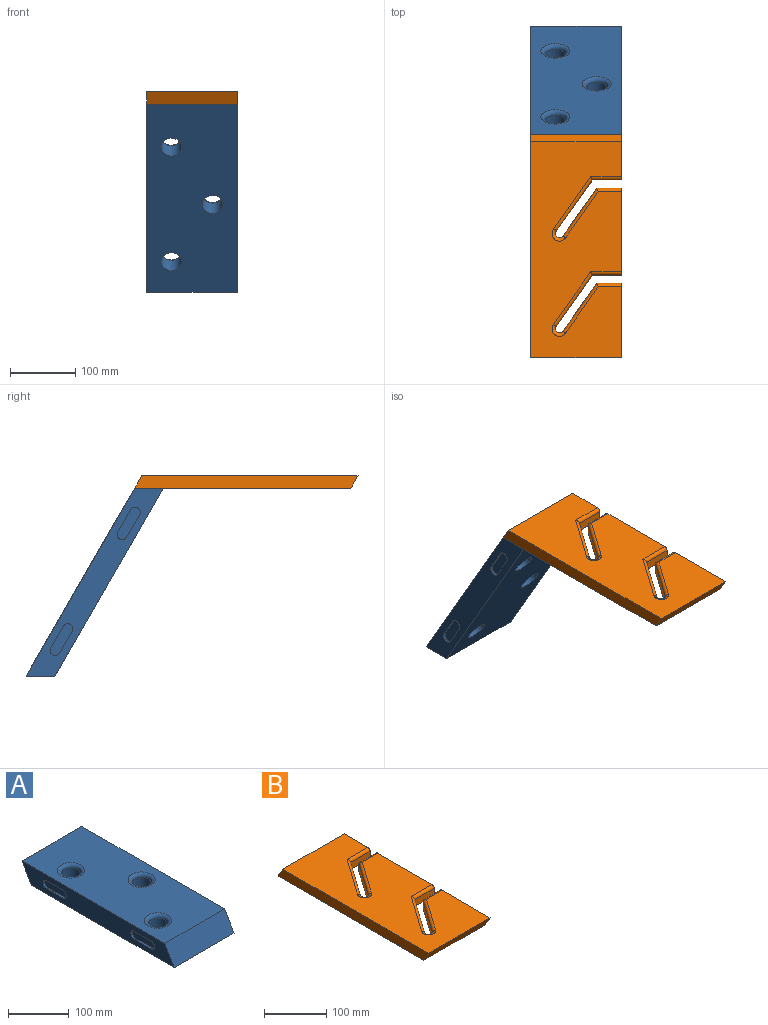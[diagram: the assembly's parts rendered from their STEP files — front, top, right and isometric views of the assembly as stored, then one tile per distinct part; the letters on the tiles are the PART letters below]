
ASSEMBLY  parts=2 mates=1
PART A: 22 faces, bbox 139.7x355.6x38.1 mm
  f0: plane 355.6x38.1mm, normal (-1,0,0), area 11085.4mm2, adj f1,f3,f4,f5,f6,f7,f8,f9
  f1: plane 333.6x139.7mm, normal (0,0,-1), area 44229.1mm2, adj f0,f2,f4,f5,f16,f17,f18
  f2: plane 355.6x38.1mm, normal (1,0,0), area 12710.3mm2, adj f1,f3,f4,f5
  f3: plane 333.6x139.7mm, normal (0,0,1), area 41949mm2, adj f0,f2,f4,f5,f19,f20,f21
  f4: plane 139.7x38.1mm, normal (0,-0.87,0.5), area 6146mm2, adj f0,f1,f2,f3
  f5: plane 139.7x38.1mm, normal (0,0.87,-0.5), area 6146mm2, adj f0,f1,f2,f3
  f6: cylinder r=7.95mm len=15.9mm, axis (-1,0,0), area 83mm2, adj f0,f7,f9,f10
  f7: plane 38.1x3.18mm, normal (0,0,1), area 121mm2, adj f0,f6,f8,f10
  f8: cylinder r=7.95mm len=15.9mm, axis (-1,0,0), area 83mm2, adj f0,f7,f9,f10
  f9: plane 38.1x3.18mm, normal (0,0,-1), area 121mm2, adj f0,f6,f8,f10
  f10: plane 55.17x15.91mm, normal (-1,0,0), area 821.4mm2, adj f6,f7,f8,f9
  f11: cylinder r=7.94mm len=15.88mm, axis (-1,0,0), area 79.1mm2, adj f0,f12,f14,f15
  f12: plane 38.1x3.18mm, normal (0,0,1), area 121mm2, adj f0,f11,f13,f15
  f13: cylinder r=7.95mm len=15.9mm, axis (-1,0,0), area 79.3mm2, adj f0,f12,f14,f15
  f14: plane 38.1x3.18mm, normal (0,0,-1), area 121mm2, adj f0,f11,f13,f15
  f15: plane 53.99x15.9mm, normal (-1,0,0), area 803.6mm2, adj f11,f12,f13,f14
  f16: cylinder r=15.88mm len=31.75mm, axis (0,0,1), area 3166.9mm2, adj f1,f19
  f17: cylinder r=15.88mm len=31.75mm, axis (0,0,1), area 3166.9mm2, adj f1,f20
  f18: cylinder r=15.88mm len=31.75mm, axis (0,0,1), area 3166.9mm2, adj f1,f21
  f19: torus R=22.23mm, axis (0,0,1), area 1139.5mm2, adj f3,f16
  f20: torus R=22.23mm, axis (0,0,1), area 1139.5mm2, adj f3,f17
  f21: torus R=22.23mm, axis (0,0,1), area 1139.5mm2, adj f3,f18
PART B: 28 faces, bbox 139.7x342.9x19.1 mm
  f0: plane 331.9x139.7mm, normal (0,0,1), area 39804.1mm2, adj f2,f3,f5,f6,f7,f8,f18,f19
  f1: cylinder r=6.35mm len=13.97mm, axis (0,0,1), area 291.5mm2, adj f4,f16,f17,f25
  f2: plane 114.3x19.05mm, normal (1,0,0), area 2067.1mm2, adj f0,f4,f8,f13,f20
  f3: plane 133.35x19.05mm, normal (1,0,0), area 2529.2mm2, adj f0,f4,f10,f12,f18,f23
  f4: plane 331.9x139.7mm, normal (0,0,-1), area 42824.9mm2, adj f1,f2,f3,f5,f6,f7,f8,f9
  f5: plane 342.9x19.05mm, normal (-1,0,0), area 6322.7mm2, adj f0,f4,f7,f8
  f6: plane 69.85x19.05mm, normal (1,0,0), area 1220.3mm2, adj f0,f4,f7,f11,f26
  f7: plane 139.7x19.05mm, normal (0,0.87,0.5), area 3073mm2, adj f0,f4,f5,f6
  f8: plane 139.7x19.05mm, normal (0,-0.87,-0.5), area 3073mm2, adj f0,f2,f4,f5
  f9: cylinder r=6.35mm len=13.97mm, axis (0,0,1), area 278.7mm2, adj f4,f14,f15,f21
  f10: plane 38.1x13.97mm, normal (0,1,0), area 532.3mm2, adj f3,f4,f17,f23
  f11: plane 44.59x13.97mm, normal (0,-1,0), area 623mm2, adj f4,f6,f16,f26
  f12: plane 44.68x13.97mm, normal (0,-1,0), area 624.1mm2, adj f3,f4,f15,f18
  f13: plane 38.1x13.97mm, normal (0,1,0), area 532.3mm2, adj f2,f4,f14,f20
  f14: plane 73.52x51.96mm, normal (-0.82,0.58,0), area 1257.7mm2, adj f4,f9,f13,f22
  f15: plane 78.88x55.76mm, normal (0.82,-0.58,0), area 1349.5mm2, adj f4,f9,f12,f19
  f16: plane 78.18x55.26mm, normal (0.82,-0.58,0), area 1337.4mm2, adj f1,f4,f11,f27
  f17: plane 73.52x51.96mm, normal (-0.82,0.58,0), area 1257.7mm2, adj f1,f4,f10,f24
  f18: cylinder r=5.08mm len=47.31mm, axis (1,0,0), area 364.1mm2, adj f0,f3,f12,f19
  f19: cylinder r=5.08mm len=83.96mm, axis (0.58,0.82,0), area 778.5mm2, adj f0,f15,f18,f21
  f20: cylinder r=5.08mm len=38.1mm, axis (-1,0,0), area 296.4mm2, adj f0,f2,f13,f22
  f21: torus R=11.43mm, axis (0,0,1), area 205.5mm2, adj f0,f9,f19,f22
  f22: cylinder r=5.08mm len=76.45mm, axis (-0.58,-0.82,0), area 710.8mm2, adj f0,f14,f20,f21
  f23: cylinder r=5.08mm len=38.1mm, axis (-1,0,0), area 296.4mm2, adj f0,f3,f10,f24
  f24: cylinder r=5.08mm len=76.45mm, axis (-0.58,-0.82,0), area 710.8mm2, adj f0,f17,f23,f25
  f25: torus R=11.43mm, axis (0,0,1), area 213.6mm2, adj f0,f1,f24,f27
  f26: cylinder r=5.08mm len=47.22mm, axis (1,0,0), area 363.5mm2, adj f0,f6,f11,f27
  f27: cylinder r=5.08mm len=83.26mm, axis (0.58,0.82,0), area 770.6mm2, adj f0,f16,f25,f26
PLACE A rot(axis=(-1,0,0),60deg) t=(-5.06,235.8,-145.33)mm
PLACE B t=(-5.06,2.94,8.65)mm fixed
MATE parallel A.f4 <-> B.f4  axis (0,0,1) through (-5.06,152.4,-0.88)mm
